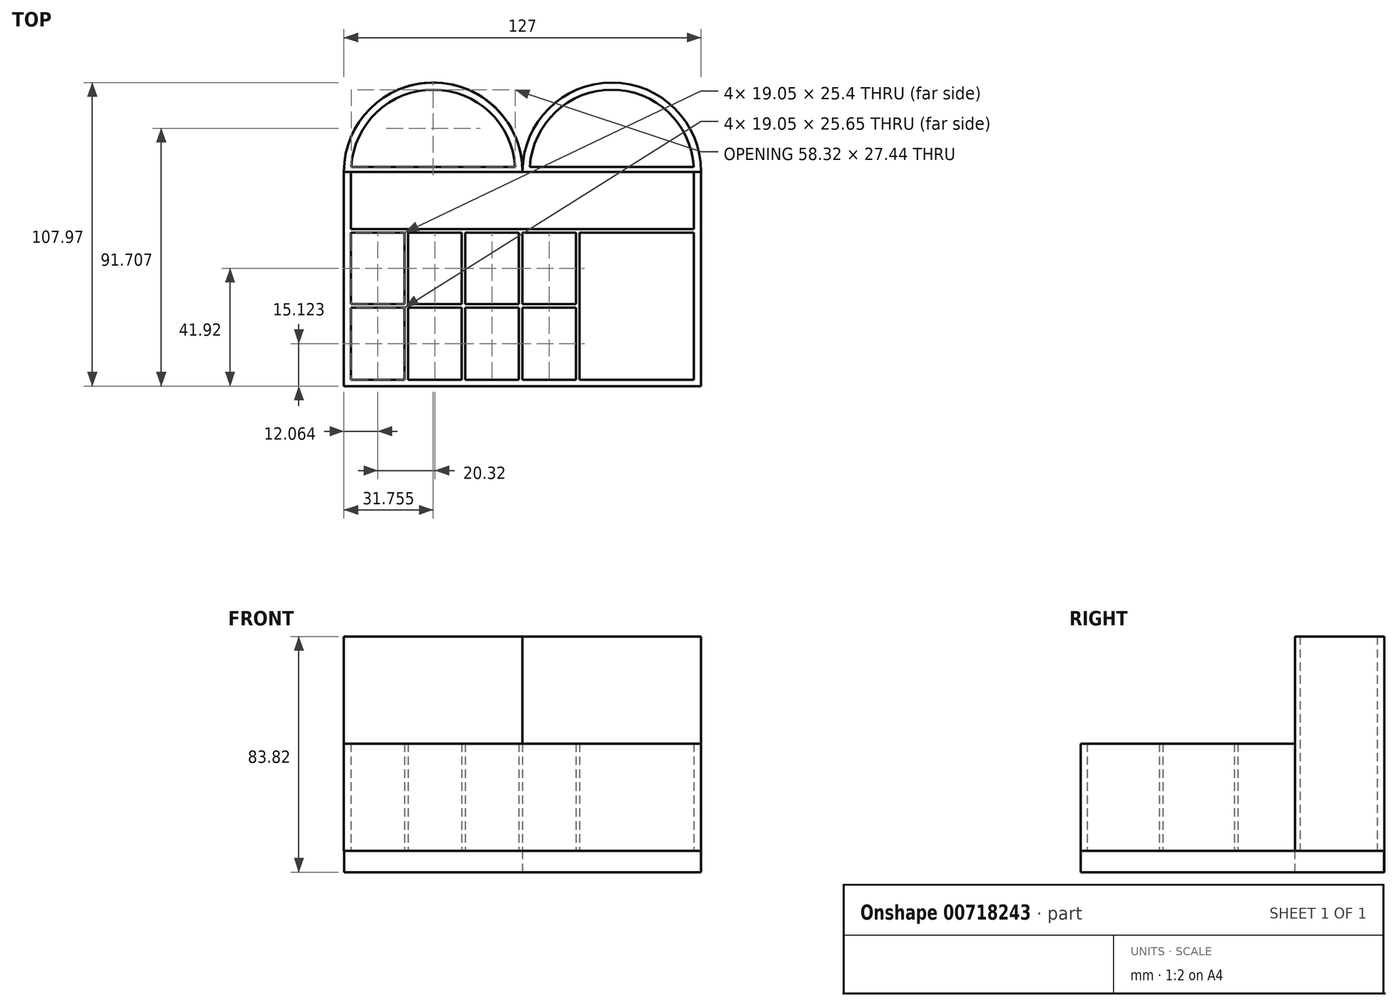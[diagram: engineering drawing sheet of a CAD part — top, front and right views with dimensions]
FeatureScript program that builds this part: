
annotation { "Feature Type Name" : "Feature", "Feature Type Description" : "" }
export const myFeature = defineFeature(function(context is Context, id is Id, definition is map)
    precondition{}
    {
        {
            var Q0;
            Q0=qCreatedBy(makeId("Top.planeOp"),FACE);
            var sketch = newSketch(context, id + "F0", { "sketchPlane" : qUnion([Q0])});
            skLineSegment(sketch, "E0.bottom", {"start": v(-159.11, 20.32) * mm, "end": v(-32.11, 20.32) * mm});
            skLineSegment(sketch, "E0.top", {"start": v(-159.11, -55.88) * mm, "end": v(-32.11, -55.88) * mm});
            skLineSegment(sketch, "E0.left", {"start": v(-159.11, 20.32) * mm, "end": v(-159.11, -55.88) * mm});
            skLineSegment(sketch, "E0.right", {"start": v(-32.11, 20.32) * mm, "end": v(-32.11, -55.88) * mm});
            skArc(sketch, "E1", {"start": v(-95.61, 20.32) * mm, "mid": v(-127.36, 52.07) * mm, "end": v(-159.11, 20.32) * mm});
            skArc(sketch, "E2", {"start": v(-32.11, 20.32) * mm, "mid": v(-63.86, 52.07) * mm, "end": v(-95.61, 20.32) * mm});
            skLineSegment(sketch, "E3", {"start": v(-156.57, 20.32) * mm, "end": v(-156.57, -55.88) * mm});
            skLineSegment(sketch, "E4", {"start": v(-34.65, 20.32) * mm, "end": v(-34.65, -55.88) * mm});
            skLineSegment(sketch, "E5", {"start": v(-159.11, 22.1) * mm, "end": v(-32.11, 22.1) * mm});
            skLineSegment(sketch, "E6", {"start": v(-159.11, 0) * mm, "end": v(-32.11, 0) * mm});
            skLineSegment(sketch, "E7", {"start": v(-156.57, -1.27) * mm, "end": v(-34.65, -1.27) * mm});
            skLineSegment(sketch, "E8", {"start": v(-156.57, -53.6) * mm, "end": v(-34.65, -53.6) * mm});
            skLineSegment(sketch, "E9", {"start": v(-137.52, -1.27) * mm, "end": v(-137.52, -53.6) * mm});
            skLineSegment(sketch, "E10", {"start": v(-136.25, -1.27) * mm, "end": v(-136.25, -53.6) * mm});
            skLineSegment(sketch, "E11", {"start": v(-117.2, -1.27) * mm, "end": v(-117.2, -53.6) * mm});
            skLineSegment(sketch, "E12", {"start": v(-115.93, -1.27) * mm, "end": v(-115.93, -53.6) * mm});
            skLineSegment(sketch, "E13", {"start": v(-96.88, -1.27) * mm, "end": v(-96.88, -53.6) * mm});
            skLineSegment(sketch, "E14", {"start": v(-95.61, -1.27) * mm, "end": v(-95.61, -53.6) * mm});
            skLineSegment(sketch, "E15", {"start": v(-76.56, -1.27) * mm, "end": v(-76.56, -53.6) * mm});
            skLineSegment(sketch, "E16", {"start": v(-75.3, -1.27) * mm, "end": v(-75.3, -55.88) * mm});
            skPoint(sketch, "E17.endSnap0", {"position": v(-137.52, -27.43) * mm});
            skLineSegment(sketch, "E18", {"start": v(-156.57, -26.67) * mm, "end": v(-76.56, -26.67) * mm});
            skLineSegment(sketch, "E19", {"start": v(-156.57, -27.94) * mm, "end": v(-76.56, -27.94) * mm});
            skArc(sketch, "E20", {"start": v(-34.65, 20.32) * mm, "mid": v(-63.85, 49.52) * mm, "end": v(-93.05, 20.32) * mm});
            skArc(sketch, "E21", {"start": v(-98.14, 20.32) * mm, "mid": v(-127.36, 49.54) * mm, "end": v(-156.57, 20.32) * mm});
            skSolve(sketch);
        }
        {
            var Q0;
            {var subQ0=sQuery(id+"F0.wireOp",EDGE,"E7");var subQ5=sQuery(id+"F0.wireOp",EDGE,"E3");var subQ6=makeQuery(id+"F0.imprint","INTERSECT",VERTEX,{"derivedFrom":[subQ5,subQ0]});Q0=makeQuery(id+"F0.imprint","IMPRINT",FACE,{"disambiguationData":[TD([[makeQuery(id+"F0.imprint","IMPRINT",EDGE,{"disambiguationData":[TD([[subQ6,1.0]])],"derivedFrom":subQ5}),1.0]])]});}
            var Q1;
            {var subQ0=sQuery(id+"F0.wireOp",EDGE,"E9");var subQ1=sQuery(id+"F0.wireOp",EDGE,"E7");var subQ2=makeQuery(id+"F0.imprint","INTERSECT",VERTEX,{"derivedFrom":[subQ1,subQ0]});Q1=makeQuery(id+"F0.imprint","IMPRINT",FACE,{"disambiguationData":[TD([[makeQuery(id+"F0.imprint","IMPRINT",EDGE,{"disambiguationData":[TD([[subQ2,-1.0]])],"derivedFrom":subQ1}),-1.0]])]});}
            var Q2;
            {var subQ0=sQuery(id+"F0.wireOp",EDGE,"E9");var subQ1=sQuery(id+"F0.wireOp",EDGE,"E8");var subQ2=makeQuery(id+"F0.imprint","INTERSECT",VERTEX,{"derivedFrom":[subQ1,subQ0]});Q2=makeQuery(id+"F0.imprint","IMPRINT",FACE,{"disambiguationData":[TD([[makeQuery(id+"F0.imprint","IMPRINT",EDGE,{"disambiguationData":[TD([[subQ2,-1.0]])],"derivedFrom":subQ1}),1.0]])]});}
            var Q3;
            {var subQ0=sQuery(id+"F0.wireOp",EDGE,"E18");var subQ1=sQuery(id+"F0.wireOp",EDGE,"E10");var subQ2=makeQuery(id+"F0.imprint","INTERSECT",VERTEX,{"derivedFrom":[subQ1,subQ0]});Q3=makeQuery(id+"F0.imprint","IMPRINT",FACE,{"disambiguationData":[TD([[makeQuery(id+"F0.imprint","IMPRINT",EDGE,{"disambiguationData":[TD([[subQ2,-1.0]])],"derivedFrom":subQ1}),1.0]])]});}
            var Q4;
            {var subQ0=sQuery(id+"F0.wireOp",EDGE,"E18");var subQ1=sQuery(id+"F0.wireOp",EDGE,"E11");var subQ2=makeQuery(id+"F0.imprint","INTERSECT",VERTEX,{"derivedFrom":[subQ1,subQ0]});Q4=makeQuery(id+"F0.imprint","IMPRINT",FACE,{"disambiguationData":[TD([[makeQuery(id+"F0.imprint","IMPRINT",EDGE,{"disambiguationData":[TD([[subQ2,-1.0]])],"derivedFrom":subQ1}),1.0]])]});}
            var Q5;
            {var subQ0=sQuery(id+"F0.wireOp",EDGE,"E11");var subQ1=sQuery(id+"F0.wireOp",EDGE,"E7");var subQ2=makeQuery(id+"F0.imprint","INTERSECT",VERTEX,{"derivedFrom":[subQ1,subQ0]});Q5=makeQuery(id+"F0.imprint","IMPRINT",FACE,{"disambiguationData":[TD([[makeQuery(id+"F0.imprint","IMPRINT",EDGE,{"disambiguationData":[TD([[subQ2,-1.0]])],"derivedFrom":subQ1}),-1.0]])]});}
            var Q6;
            {var subQ0=sQuery(id+"F0.wireOp",EDGE,"E11");var subQ1=sQuery(id+"F0.wireOp",EDGE,"E8");var subQ2=makeQuery(id+"F0.imprint","INTERSECT",VERTEX,{"derivedFrom":[subQ1,subQ0]});Q6=makeQuery(id+"F0.imprint","IMPRINT",FACE,{"disambiguationData":[TD([[makeQuery(id+"F0.imprint","IMPRINT",EDGE,{"disambiguationData":[TD([[subQ2,-1.0]])],"derivedFrom":subQ1}),1.0]])]});}
            var Q7;
            {var subQ0=sQuery(id+"F0.wireOp",EDGE,"E18");var subQ1=sQuery(id+"F0.wireOp",EDGE,"E12");var subQ2=makeQuery(id+"F0.imprint","INTERSECT",VERTEX,{"derivedFrom":[subQ1,subQ0]});Q7=makeQuery(id+"F0.imprint","IMPRINT",FACE,{"disambiguationData":[TD([[makeQuery(id+"F0.imprint","IMPRINT",EDGE,{"disambiguationData":[TD([[subQ2,-1.0]])],"derivedFrom":subQ1}),1.0]])]});}
            var Q8;
            {var subQ0=sQuery(id+"F0.wireOp",EDGE,"E18");var subQ1=sQuery(id+"F0.wireOp",EDGE,"E13");var subQ2=makeQuery(id+"F0.imprint","INTERSECT",VERTEX,{"derivedFrom":[subQ1,subQ0]});Q8=makeQuery(id+"F0.imprint","IMPRINT",FACE,{"disambiguationData":[TD([[makeQuery(id+"F0.imprint","IMPRINT",EDGE,{"disambiguationData":[TD([[subQ2,-1.0]])],"derivedFrom":subQ1}),1.0]])]});}
            var Q9;
            {var subQ0=sQuery(id+"F0.wireOp",EDGE,"E13");var subQ1=sQuery(id+"F0.wireOp",EDGE,"E7");var subQ2=makeQuery(id+"F0.imprint","INTERSECT",VERTEX,{"derivedFrom":[subQ1,subQ0]});Q9=makeQuery(id+"F0.imprint","IMPRINT",FACE,{"disambiguationData":[TD([[makeQuery(id+"F0.imprint","IMPRINT",EDGE,{"disambiguationData":[TD([[subQ2,-1.0]])],"derivedFrom":subQ1}),-1.0]])]});}
            var Q10;
            {var subQ0=sQuery(id+"F0.wireOp",EDGE,"E18");var subQ1=sQuery(id+"F0.wireOp",EDGE,"E14");var subQ2=makeQuery(id+"F0.imprint","INTERSECT",VERTEX,{"derivedFrom":[subQ1,subQ0]});Q10=makeQuery(id+"F0.imprint","IMPRINT",FACE,{"disambiguationData":[TD([[makeQuery(id+"F0.imprint","IMPRINT",EDGE,{"disambiguationData":[TD([[subQ2,-1.0]])],"derivedFrom":subQ1}),1.0]])]});}
            var Q11;
            {var subQ0=sQuery(id+"F0.wireOp",EDGE,"E13");var subQ1=sQuery(id+"F0.wireOp",EDGE,"E8");var subQ2=makeQuery(id+"F0.imprint","INTERSECT",VERTEX,{"derivedFrom":[subQ1,subQ0]});Q11=makeQuery(id+"F0.imprint","IMPRINT",FACE,{"disambiguationData":[TD([[makeQuery(id+"F0.imprint","IMPRINT",EDGE,{"disambiguationData":[TD([[subQ2,-1.0]])],"derivedFrom":subQ1}),1.0]])]});}
            var Q12;
            {var subQ7=sQuery(id+"F0.wireOp",EDGE,"E3");var subQ8=sQuery(id+"F0.wireOp",EDGE,"E0.top");var subQ9=makeQuery(id+"F0.imprint","INTERSECT",VERTEX,{"derivedFrom":[subQ8,subQ7]});Q12=makeQuery(id+"F0.imprint","IMPRINT",FACE,{"disambiguationData":[TD([[makeQuery(id+"F0.imprint","IMPRINT",EDGE,{"disambiguationData":[TD([[subQ9,-1.0]])],"derivedFrom":subQ8}),1.0]])]});}
            var Q13;
            {var subQ0=sQuery(id+"F0.wireOp",EDGE,"E4");var subQ1=sQuery(id+"F0.wireOp",EDGE,"E0.top");var subQ2=makeQuery(id+"F0.imprint","INTERSECT",VERTEX,{"derivedFrom":[subQ1,subQ0]});Q13=makeQuery(id+"F0.imprint","IMPRINT",FACE,{"disambiguationData":[TD([[makeQuery(id+"F0.imprint","IMPRINT",EDGE,{"disambiguationData":[TD([[subQ2,1.0]])],"derivedFrom":subQ1}),1.0]])]});}
            var Q14;
            {var subQ0=sQuery(id+"F0.wireOp",EDGE,"E15");var subQ1=sQuery(id+"F0.wireOp",EDGE,"E7");var subQ2=makeQuery(id+"F0.imprint","INTERSECT",VERTEX,{"derivedFrom":[subQ1,subQ0]});Q14=makeQuery(id+"F0.imprint","IMPRINT",FACE,{"disambiguationData":[TD([[makeQuery(id+"F0.imprint","IMPRINT",EDGE,{"disambiguationData":[TD([[subQ2,-1.0]])],"derivedFrom":subQ1}),-1.0]])]});}
            var Q15;
            {var subQ5=sQuery(id+"F0.wireOp",EDGE,"E0.right");var subQ7=sQuery(id+"F0.wireOp",EDGE,"E0.top");var subQ8=makeQuery(id+"F0.imprint","INTERSECT",VERTEX,{"derivedFrom":[subQ7,subQ5]});Q15=makeQuery(id+"F0.imprint","IMPRINT",FACE,{"disambiguationData":[TD([[makeQuery(id+"F0.imprint","IMPRINT",EDGE,{"disambiguationData":[TD([[subQ8,1.0]])],"derivedFrom":subQ7}),1.0]])]});}
            var Q16;
            {var subQ0=sQuery(id+"F0.wireOp",EDGE,"E0.right");var subQ5=sQuery(id+"F0.wireOp",EDGE,"E6");var subQ6=makeQuery(id+"F0.imprint","INTERSECT",VERTEX,{"derivedFrom":[subQ0,subQ5]});Q16=makeQuery(id+"F0.imprint","IMPRINT",FACE,{"disambiguationData":[TD([[makeQuery(id+"F0.imprint","IMPRINT",EDGE,{"disambiguationData":[TD([[subQ6,1.0]])],"derivedFrom":subQ5}),1.0]])]});}
            var Q17;
            {var subQ0=sQuery(id+"F0.wireOp",EDGE,"E0.left");var subQ5=sQuery(id+"F0.wireOp",EDGE,"E6");var subQ6=makeQuery(id+"F0.imprint","INTERSECT",VERTEX,{"derivedFrom":[subQ0,subQ5]});Q17=makeQuery(id+"F0.imprint","IMPRINT",FACE,{"disambiguationData":[TD([[makeQuery(id+"F0.imprint","IMPRINT",EDGE,{"disambiguationData":[TD([[subQ6,-1.0]])],"derivedFrom":subQ5}),1.0]])]});}
            var Q18;
            {var subQ3=sQuery(id+"F0.wireOp",EDGE,"E0.left");var subQ4=sQuery(id+"F0.wireOp",EDGE,"E0.top");var subQ5=makeQuery(id+"F0.imprint","INTERSECT",VERTEX,{"derivedFrom":[subQ4,subQ3]});Q18=makeQuery(id+"F0.imprint","IMPRINT",FACE,{"disambiguationData":[TD([[makeQuery(id+"F0.imprint","IMPRINT",EDGE,{"disambiguationData":[TD([[subQ5,-1.0]])],"derivedFrom":subQ4}),1.0]])]});}
            var Q19;
            {var subQ0=sQuery(id+"F0.wireOp",EDGE,"E18");var subQ1=sQuery(id+"F0.wireOp",EDGE,"E3");var subQ2=makeQuery(id+"F0.imprint","INTERSECT",VERTEX,{"derivedFrom":[subQ1,subQ0]});Q19=makeQuery(id+"F0.imprint","IMPRINT",FACE,{"disambiguationData":[TD([[makeQuery(id+"F0.imprint","IMPRINT",EDGE,{"disambiguationData":[TD([[subQ2,-1.0]])],"derivedFrom":subQ1}),1.0]])]});}
            var Q20;
            {var subQ0=sQuery(id+"F0.wireOp",EDGE,"E18");var subQ1=sQuery(id+"F0.wireOp",EDGE,"E9");var subQ2=makeQuery(id+"F0.imprint","INTERSECT",VERTEX,{"derivedFrom":[subQ1,subQ0]});Q20=makeQuery(id+"F0.imprint","IMPRINT",FACE,{"disambiguationData":[TD([[makeQuery(id+"F0.imprint","IMPRINT",EDGE,{"disambiguationData":[TD([[subQ2,-1.0]])],"derivedFrom":subQ1}),1.0]])]});}
            extrude(context, id + "F1", {"entities" : qUnion([Q0, Q1, Q2, Q3, Q4, Q5, Q6, Q7, Q8, Q9, Q10, Q11, Q12, Q13, Q14, Q15, Q16, Q17, Q18, Q19, Q20]), "depth" : 38.1 * mm, "offsetDistance" : 25.4 * mm});
        }
        {
            var Q0;
            {var subQ0=sQuery(id+"F0.wireOp",EDGE,"E21");var subQ4=sQuery(id+"F0.wireOp",EDGE,"E5");var subQ5=makeQuery(id+"F0.imprint","INTERSECT",VERTEX,{"disambiguationData":[OD(0.0)],"derivedFrom":[subQ4,subQ0]});Q0=makeQuery(id+"F0.imprint","IMPRINT",FACE,{"disambiguationData":[TD([[makeQuery(id+"F0.imprint","IMPRINT",EDGE,{"disambiguationData":[TD([[subQ5,-1.0]])],"derivedFrom":subQ4}),-1.0]])]});}
            var Q1;
            {var subQ0=sQuery(id+"F0.wireOp",EDGE,"E2");var subQ5=sQuery(id+"F0.wireOp",EDGE,"E5");var subQ6=makeQuery(id+"F0.imprint","INTERSECT",VERTEX,{"disambiguationData":[OD(1.0)],"derivedFrom":[subQ0,subQ5]});Q1=makeQuery(id+"F0.imprint","IMPRINT",FACE,{"disambiguationData":[TD([[makeQuery(id+"F0.imprint","IMPRINT",EDGE,{"disambiguationData":[TD([[subQ6,-1.0]])],"derivedFrom":subQ5}),-1.0]])]});}
            var Q2;
            {var subQ0=sQuery(id+"F0.wireOp",EDGE,"E1");var subQ5=sQuery(id+"F0.wireOp",EDGE,"E5");var subQ6=makeQuery(id+"F0.imprint","INTERSECT",VERTEX,{"disambiguationData":[OD(1.0)],"derivedFrom":[subQ0,subQ5]});Q2=makeQuery(id+"F0.imprint","IMPRINT",FACE,{"disambiguationData":[TD([[makeQuery(id+"F0.imprint","IMPRINT",EDGE,{"disambiguationData":[TD([[subQ6,1.0]])],"derivedFrom":subQ5}),-1.0]])]});}
            var Q3;
            {var subQ0=sQuery(id+"F0.wireOp",EDGE,"E5");var subQ1=sQuery(id+"F0.wireOp",EDGE,"E1");var subQ2=makeQuery(id+"F0.imprint","INTERSECT",VERTEX,{"disambiguationData":[OD(0.0)],"derivedFrom":[subQ1,subQ0]});Q3=makeQuery(id+"F0.imprint","IMPRINT",FACE,{"disambiguationData":[TD([[makeQuery(id+"F0.imprint","IMPRINT",EDGE,{"disambiguationData":[TD([[subQ2,1.0]])],"derivedFrom":subQ1}),1.0]])]});}
            var Q4;
            {var subQ0=sQuery(id+"F0.wireOp",EDGE,"E5");var subQ1=sQuery(id+"F0.wireOp",EDGE,"E2");var subQ2=makeQuery(id+"F0.imprint","INTERSECT",VERTEX,{"disambiguationData":[OD(0.0)],"derivedFrom":[subQ1,subQ0]});Q4=makeQuery(id+"F0.imprint","IMPRINT",FACE,{"disambiguationData":[TD([[makeQuery(id+"F0.imprint","IMPRINT",EDGE,{"disambiguationData":[TD([[subQ2,-1.0]])],"derivedFrom":subQ1}),1.0]])]});}
            var Q5;
            {var subQ0=sQuery(id+"F0.wireOp",EDGE,"E20");var subQ4=sQuery(id+"F0.wireOp",EDGE,"E5");var subQ5=makeQuery(id+"F0.imprint","INTERSECT",VERTEX,{"disambiguationData":[OD(0.0)],"derivedFrom":[subQ4,subQ0]});Q5=makeQuery(id+"F0.imprint","IMPRINT",FACE,{"disambiguationData":[TD([[makeQuery(id+"F0.imprint","IMPRINT",EDGE,{"disambiguationData":[TD([[subQ5,-1.0]])],"derivedFrom":subQ4}),-1.0]])]});}
            var Q6;
            {var subQ0=sQuery(id+"F0.wireOp",EDGE,"E1");var subQ5=sQuery(id+"F0.wireOp",EDGE,"E5");var subQ6=makeQuery(id+"F0.imprint","INTERSECT",VERTEX,{"disambiguationData":[OD(0.0)],"derivedFrom":[subQ0,subQ5]});Q6=makeQuery(id+"F0.imprint","IMPRINT",FACE,{"disambiguationData":[TD([[makeQuery(id+"F0.imprint","IMPRINT",EDGE,{"disambiguationData":[TD([[subQ6,-1.0]])],"derivedFrom":subQ5}),-1.0]])]});}
            var Q7;
            {var subQ0=sQuery(id+"F0.wireOp",EDGE,"E2");var subQ5=sQuery(id+"F0.wireOp",EDGE,"E5");var subQ7=makeQuery(id+"F0.imprint","INTERSECT",VERTEX,{"disambiguationData":[OD(0.0)],"derivedFrom":[subQ0,subQ5]});Q7=makeQuery(id+"F0.imprint","IMPRINT",FACE,{"disambiguationData":[TD([[makeQuery(id+"F0.imprint","IMPRINT",EDGE,{"disambiguationData":[TD([[subQ7,1.0]])],"derivedFrom":subQ5}),-1.0]])]});}
            extrude(context, id + "F2", {"entities" : qUnion([Q0, Q1, Q2, Q3, Q4, Q5, Q6, Q7]), "depth" : 76.2 * mm, "offsetDistance" : 25.4 * mm});
        }
        {
            var Q0;
            Q0=qCreatedBy(makeId("Top.planeOp"),FACE);
            var sketch = newSketch(context, id + "F3", { "sketchPlane" : qUnion([Q0])});
            skLineSegment(sketch, "E22", {"start": v(-159.09, 20.33) * mm, "end": v(-159.09, -55.9) * mm});
            skLineSegment(sketch, "E23", {"start": v(-159.09, -55.9) * mm, "end": v(-32.12, -55.9) * mm});
            skLineSegment(sketch, "E24", {"start": v(-32.12, -55.9) * mm, "end": v(-32.12, 20.26) * mm});
            skArc(sketch, "E25", {"start": v(-95.58, 20.33) * mm, "mid": v(-127.33, 52.08) * mm, "end": v(-159.09, 20.33) * mm});
            skArc(sketch, "E26", {"start": v(-32.12, 20.26) * mm, "mid": v(-63.82, 52) * mm, "end": v(-95.58, 20.33) * mm});
            skSolve(sketch);
        }
        {
            var Q0;
            Q0 = qSketchRegion(id + "F3", true);
            extrude(context, id + "F4", {"entities" : qUnion([Q0]), "oppositeDirection" : true, "depth" : 7.62 * mm, "offsetDistance" : 25.4 * mm});
        }
    });
